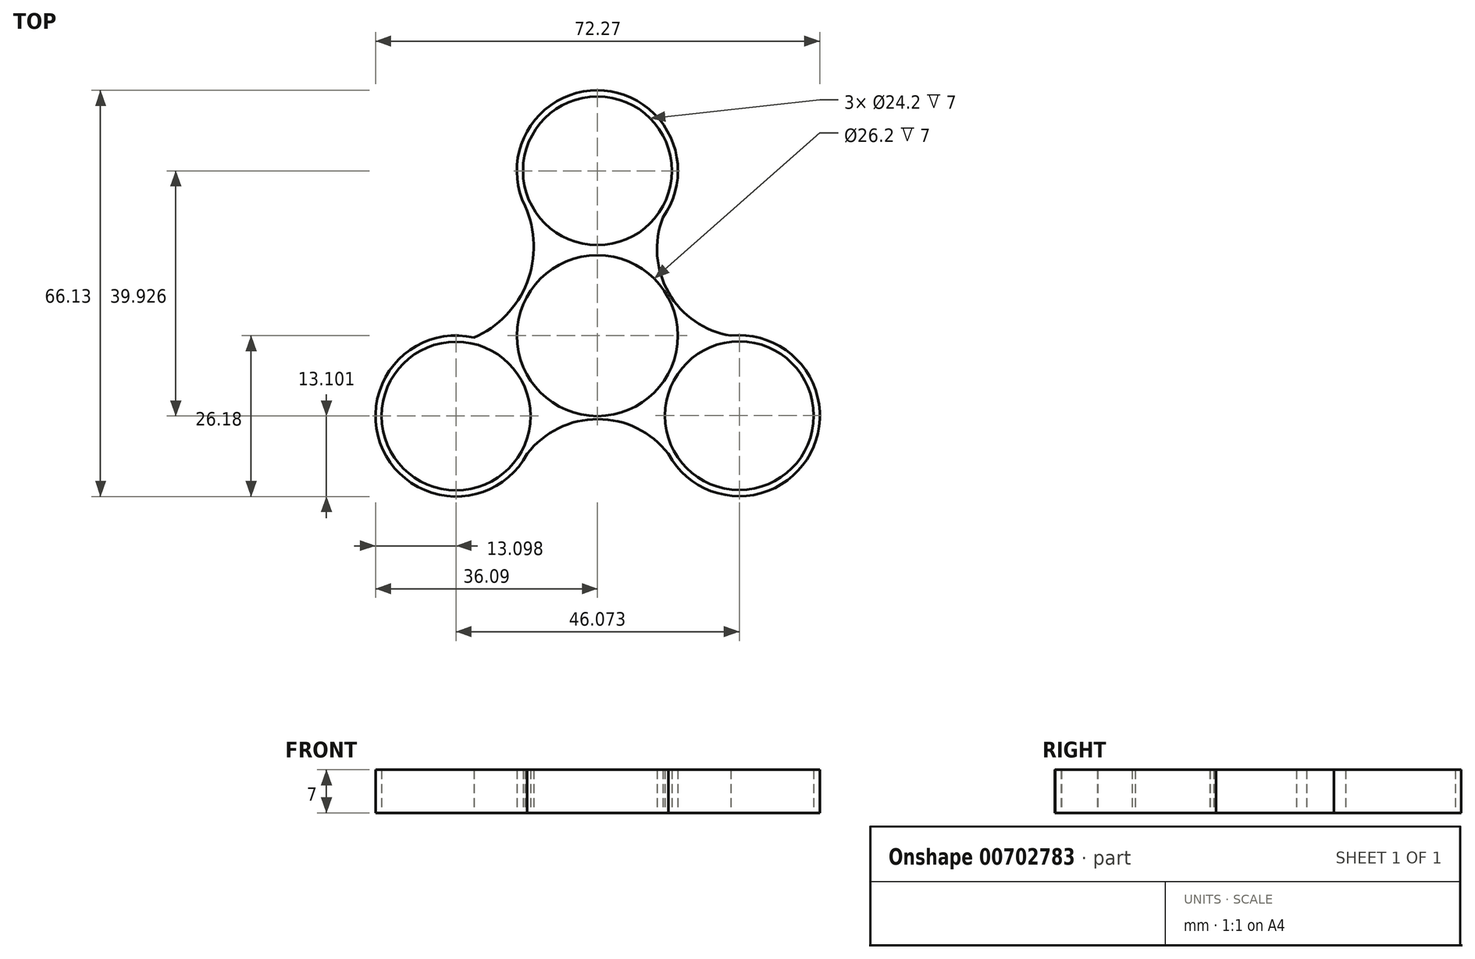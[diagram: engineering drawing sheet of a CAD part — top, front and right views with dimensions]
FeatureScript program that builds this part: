
annotation { "Feature Type Name" : "Feature", "Feature Type Description" : "" }
export const myFeature = defineFeature(function(context is Context, id is Id, definition is map)
    precondition{}
    {
        {
            var Q0;
            Q0=qCreatedBy(makeId("Top.planeOp"),FACE);
            var sketch = newSketch(context, id + "F0", { "sketchPlane" : qUnion([Q0])});
            skCircle(sketch, "E0", {"center": v(0, 0) * mm, "radius": 12.1 * mm});
            skCircle(sketch, "E1", {"center": v(0, 26.85) * mm, "radius": 12.1 * mm});
            skCircle(sketch, "E2.1.0", {"center": v(-23, -13.08) * mm, "radius": 12.1 * mm});
            skCircle(sketch, "E2.2.0", {"center": v(23.08, -13.03) * mm, "radius": 12.1 * mm});
            skPoint(sketch, "E2.center", {"position": v(0.03, 0.25) * mm});
            skCircle(sketch, "E3", {"center": v(0, 0) * mm, "radius": 13.1 * mm});
            skCircle(sketch, "E4", {"center": v(23.08, -13.03) * mm, "radius": 13.1 * mm});
            skCircle(sketch, "E5", {"center": v(-23, -13.08) * mm, "radius": 13.1 * mm});
            skCircle(sketch, "E6", {"center": v(0, 26.85) * mm, "radius": 13.1 * mm});
            skArc(sketch, "E7", {"start": v(10.67, 19.24) * mm, "mid": v(11.58, 6.98) * mm, "end": v(21.7, 0) * mm});
            skArc(sketch, "E8", {"start": v(-20.1, -0.3) * mm, "mid": v(-11.44, 8.65) * mm, "end": v(-11.77, 21.1) * mm});
            skArc(sketch, "E9", {"start": v(11.54, -19.22) * mm, "mid": v(0.06, -13.58) * mm, "end": v(-11.42, -19.23) * mm});
            skSolve(sketch);
        }
        {
            var Q0;
            Q0 = qSketchRegion(id + "F0", true);
            extrude(context, id + "F1", {"entities" : qUnion([Q0]), "depth" : 7 * mm, "offsetDistance" : 25 * mm});
        }
    });
